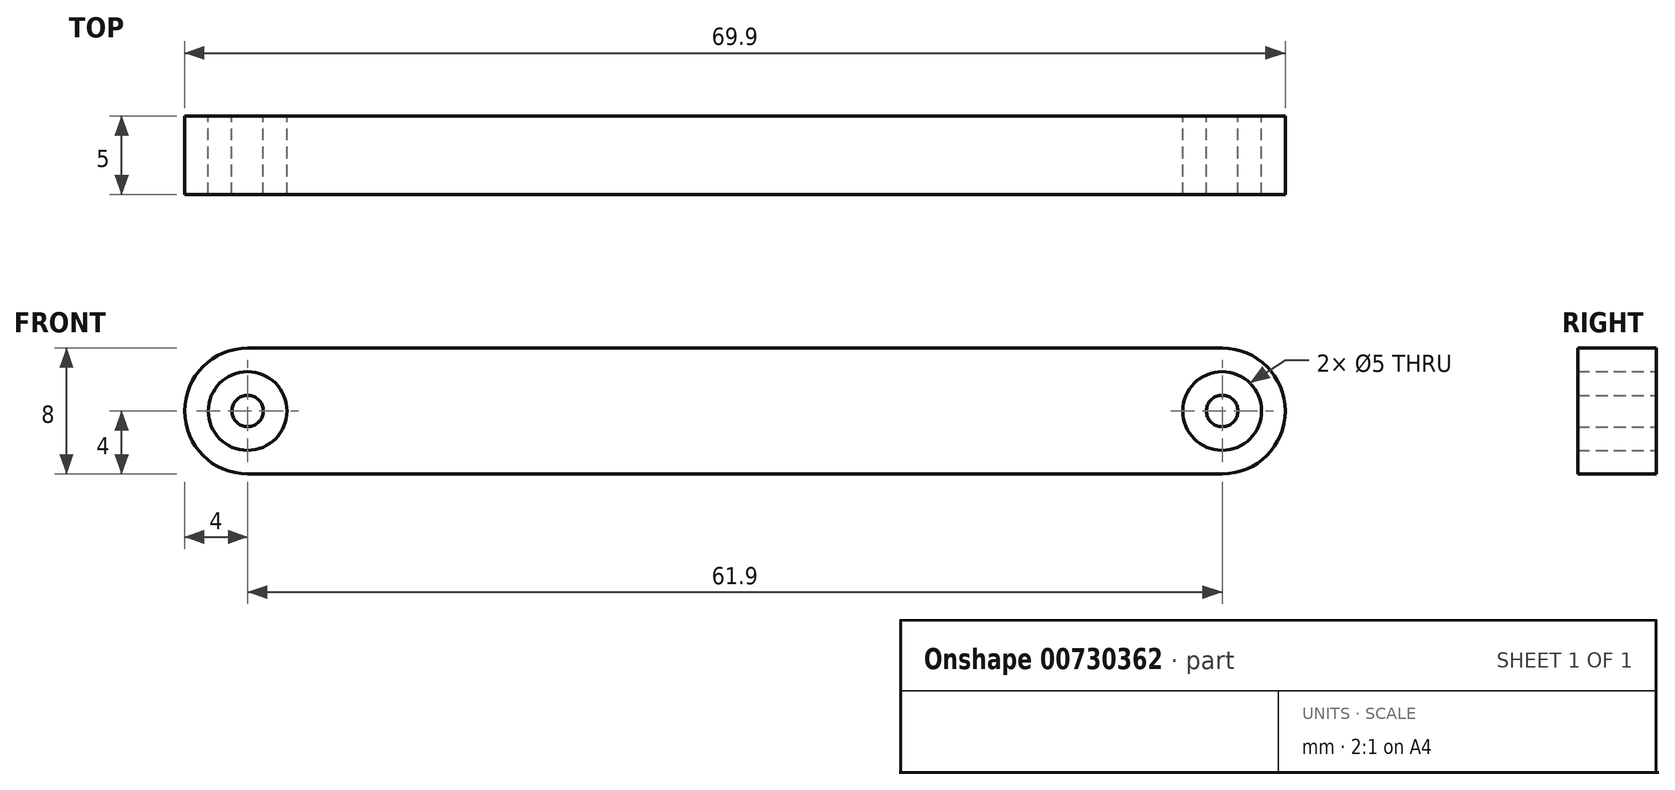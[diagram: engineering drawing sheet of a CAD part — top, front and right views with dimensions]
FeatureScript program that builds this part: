
annotation { "Feature Type Name" : "Feature", "Feature Type Description" : "" }
export const myFeature = defineFeature(function(context is Context, id is Id, definition is map)
    precondition{}
    {
        {
            var Q0;
            Q0=qCreatedBy(makeId("Front.planeOp"),FACE);
            var sketch = newSketch(context, id + "F0", { "sketchPlane" : qUnion([Q0])});
            skArc(sketch, "E0", {"start": v(0, 4) * mm, "mid": v(-4, 0) * mm, "end": v(0, -4) * mm});
            skCircle(sketch, "E1", {"center": v(0, 0) * mm, "radius": 2.5 * mm});
            skCircle(sketch, "E2", {"center": v(0, 0) * mm, "radius": 1 * mm});
            skArc(sketch, "E3", {"start": v(61.9, -4) * mm, "mid": v(65.9, 0) * mm, "end": v(61.9, 4) * mm});
            skCircle(sketch, "E4", {"center": v(61.9, 0) * mm, "radius": 2.5 * mm});
            skCircle(sketch, "E5", {"center": v(61.9, 0) * mm, "radius": 1 * mm});
            skLineSegment(sketch, "E6", {"start": v(0, 4) * mm, "end": v(61.9, 4) * mm});
            skLineSegment(sketch, "E7", {"start": v(0, -4) * mm, "end": v(61.9, -4) * mm});
            skSolve(sketch);
        }
        {
            var Q0;
            Q0 = qSketchRegion(id + "F0", true);
            var Q1;
            Q1=makeQuery(id+"F0.imprint","IMPRINT",FACE,{"disambiguationData":[TD([[makeQuery(id+"F0.imprint","IMPRINT",EDGE,{"derivedFrom":sQuery(id+"F0.wireOp",EDGE,"E2")}),1.0]])]});
            var Q2;
            Q2=makeQuery(id+"F0.imprint","IMPRINT",FACE,{"disambiguationData":[TD([[makeQuery(id+"F0.imprint","IMPRINT",EDGE,{"derivedFrom":sQuery(id+"F0.wireOp",EDGE,"E5")}),1.0]])]});
            extrude(context, id + "F1", {"entities" : qUnion([Q0, Q1, Q2]), "depth" : 5 * mm, "offsetDistance" : 25 * mm});
        }
    });
